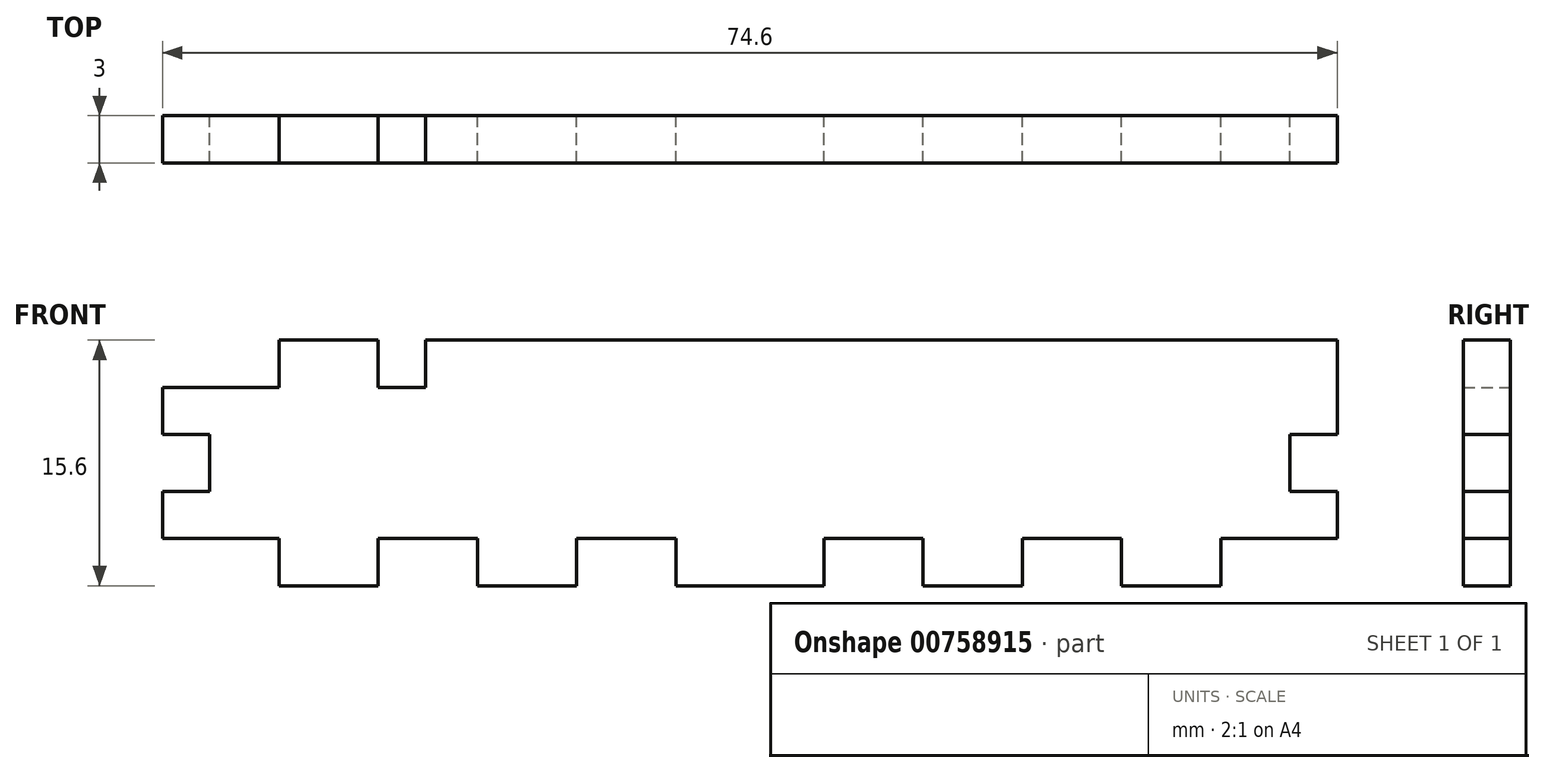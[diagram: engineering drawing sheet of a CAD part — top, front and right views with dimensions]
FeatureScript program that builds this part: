
annotation { "Feature Type Name" : "Feature", "Feature Type Description" : "" }
export const myFeature = defineFeature(function(context is Context, id is Id, definition is map)
    precondition{}
    {
        {
            var Q0;
            Q0=qCreatedBy(makeId("Front.planeOp"),FACE);
            var sketch = newSketch(context, id + "F0", { "sketchPlane" : qUnion([Q0])});
            skLineSegment(sketch, "E0.0.0", {"start": v(-32.6, -12.6) * mm, "end": v(-32.6, -15.6) * mm});
            skLineSegment(sketch, "E0.0.1", {"start": v(-32.6, -15.6) * mm, "end": v(-42, -15.6) * mm});
            skLineSegment(sketch, "E0.0.2", {"start": v(-42, -15.6) * mm, "end": v(-42, -12.6) * mm});
            skLineSegment(sketch, "E0.0.3", {"start": v(-42, -12.6) * mm, "end": v(-48.3, -12.6) * mm});
            skLineSegment(sketch, "E0.0.4", {"start": v(-48.3, -12.6) * mm, "end": v(-48.3, -15.6) * mm});
            skLineSegment(sketch, "E0.0.5", {"start": v(-48.3, -15.6) * mm, "end": v(-54.6, -15.6) * mm});
            skLineSegment(sketch, "E0.0.6", {"start": v(-54.6, -15.6) * mm, "end": v(-54.6, -12.6) * mm});
            skLineSegment(sketch, "E0.0.7", {"start": v(-54.6, -12.6) * mm, "end": v(-60.9, -12.6) * mm});
            skLineSegment(sketch, "E0.0.8", {"start": v(-60.9, -12.6) * mm, "end": v(-60.9, -15.6) * mm});
            skLineSegment(sketch, "E0.0.9", {"start": v(-60.9, -15.6) * mm, "end": v(-67.2, -15.6) * mm});
            skLineSegment(sketch, "E0.0.10", {"start": v(-67.2, -15.6) * mm, "end": v(-67.2, -12.6) * mm});
            skLineSegment(sketch, "E0.0.11", {"start": v(-67.2, -12.6) * mm, "end": v(-74.6, -12.6) * mm});
            skLineSegment(sketch, "E0.0.12", {"start": v(-74.6, -12.6) * mm, "end": v(-74.6, -9.6) * mm});
            skLineSegment(sketch, "E0.0.13", {"start": v(-74.6, -9.6) * mm, "end": v(-71.6, -9.6) * mm});
            skLineSegment(sketch, "E0.0.14", {"start": v(-71.6, -9.6) * mm, "end": v(-71.6, -6) * mm});
            skLineSegment(sketch, "E0.0.15", {"start": v(-71.6, -6) * mm, "end": v(-74.6, -6) * mm});
            skLineSegment(sketch, "E0.0.16", {"start": v(-74.6, -6) * mm, "end": v(-74.6, -3) * mm});
            skLineSegment(sketch, "E0.0.17", {"start": v(-74.6, -3) * mm, "end": v(-67.2, -3) * mm});
            skLineSegment(sketch, "E0.0.18", {"start": v(-67.2, -3) * mm, "end": v(-67.2, 0) * mm});
            skLineSegment(sketch, "E0.0.19", {"start": v(-67.2, 0) * mm, "end": v(-60.9, 0) * mm});
            skLineSegment(sketch, "E0.0.20", {"start": v(-60.9, 0) * mm, "end": v(-60.9, -3) * mm});
            skLineSegment(sketch, "E0.0.28", {"start": v(0, 0) * mm, "end": v(0, -6) * mm});
            skLineSegment(sketch, "E0.0.29", {"start": v(0, -6) * mm, "end": v(-3, -6) * mm});
            skLineSegment(sketch, "E0.0.30", {"start": v(-3, -6) * mm, "end": v(-3, -9.6) * mm});
            skLineSegment(sketch, "E0.0.31", {"start": v(-3, -9.6) * mm, "end": v(0, -9.6) * mm});
            skLineSegment(sketch, "E0.0.32", {"start": v(0, -9.6) * mm, "end": v(0, -12.6) * mm});
            skLineSegment(sketch, "E0.0.33", {"start": v(0, -12.6) * mm, "end": v(-7.4, -12.6) * mm});
            skLineSegment(sketch, "E0.0.34", {"start": v(-7.4, -12.6) * mm, "end": v(-7.4, -15.6) * mm});
            skLineSegment(sketch, "E0.0.35", {"start": v(-7.4, -15.6) * mm, "end": v(-13.7, -15.6) * mm});
            skLineSegment(sketch, "E0.0.36", {"start": v(-13.7, -15.6) * mm, "end": v(-13.7, -12.6) * mm});
            skLineSegment(sketch, "E0.0.37", {"start": v(-13.7, -12.6) * mm, "end": v(-20, -12.6) * mm});
            skLineSegment(sketch, "E0.0.38", {"start": v(-20, -12.6) * mm, "end": v(-20, -15.6) * mm});
            skLineSegment(sketch, "E0.0.39", {"start": v(-20, -15.6) * mm, "end": v(-26.3, -15.6) * mm});
            skLineSegment(sketch, "E0.0.40", {"start": v(-26.3, -15.6) * mm, "end": v(-26.3, -12.6) * mm});
            skLineSegment(sketch, "E0.0.41", {"start": v(-26.3, -12.6) * mm, "end": v(-32.6, -12.6) * mm});
            skLineSegment(sketch, "E1", {"start": v(-60.9, -3) * mm, "end": v(-57.9, -3) * mm});
            skLineSegment(sketch, "E2", {"start": v(-57.9, -3) * mm, "end": v(-57.9, 0) * mm});
            skLineSegment(sketch, "E3", {"start": v(-57.9, 0) * mm, "end": v(0, 0) * mm});
            skSolve(sketch);
        }
        {
            var Q0;
            Q0 = qSketchRegion(id + "F0", true);
            extrude(context, id + "F1", {"entities" : qUnion([Q0]), "depth" : 3 * mm, "offsetDistance" : 25 * mm});
        }
    });
